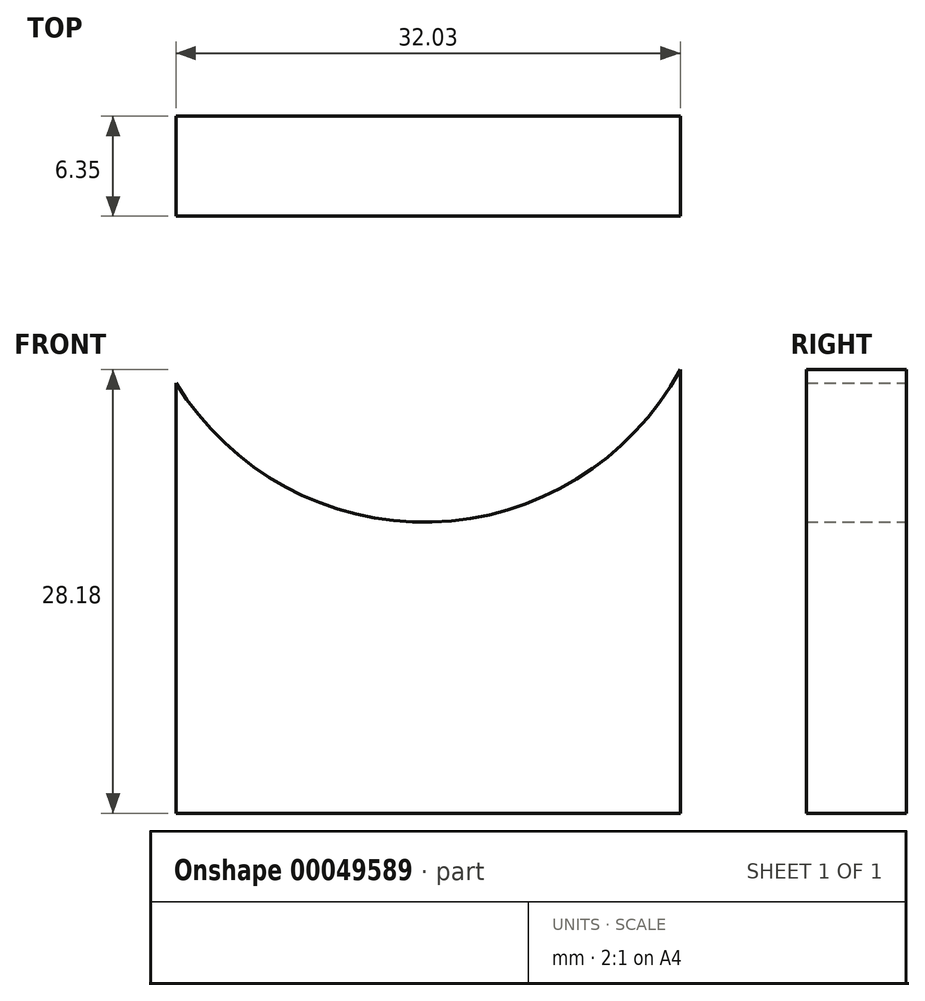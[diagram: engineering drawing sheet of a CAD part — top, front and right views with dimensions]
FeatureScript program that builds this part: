
annotation { "Feature Type Name" : "Feature", "Feature Type Description" : "" }
export const myFeature = defineFeature(function(context is Context, id is Id, definition is map)
    precondition{}
    {
        {
            var Q0;
            Q0=qCreatedBy(makeId("Front.planeOp"),FACE);
            var sketch = newSketch(context, id + "F0", { "sketchPlane" : qUnion([Q0])});
            skLineSegment(sketch, "E0.bottom", {"start": v(-15.77, 29.39) * mm, "end": v(16.26, 29.39) * mm});
            skLineSegment(sketch, "E0.top", {"start": v(-15.77, -7.61) * mm, "end": v(16.26, -7.61) * mm});
            skLineSegment(sketch, "E0.left", {"start": v(-15.77, 29.39) * mm, "end": v(-15.77, -7.61) * mm});
            skLineSegment(sketch, "E0.right", {"start": v(16.26, 29.39) * mm, "end": v(16.26, -7.61) * mm});
            skLineSegment(sketch, "E1", {"start": v(-26.81, -7.61) * mm, "end": v(-26.81, 11.59) * mm});
            skPoint(sketch, "E2", {"position": v(0, 10.89) * mm});
            skPoint(sketch, "E3", {"position": v(-15.77, 10.89) * mm});
            skCircle(sketch, "E4", {"center": v(0, 29.39) * mm, "radius": 18.5 * mm});
            skPoint(sketch, "E5", {"position": v(0.25, 29.39) * mm});
            skSolve(sketch);
        }
        {
            var Q0;
            {var subQ5=sQuery(id+"F0.wireOp",EDGE,"E0.top");Q0=makeQuery(id+"F0.imprint","IMPRINT",FACE,{"disambiguationData":[TD([[makeQuery(id+"F0.imprint","IMPRINT",EDGE,{"derivedFrom":subQ5}),1.0]])]});}
            extrude(context, id + "F1", {"entities" : qUnion([Q0]), "depth" : 6.35 * mm});
        }
    });
